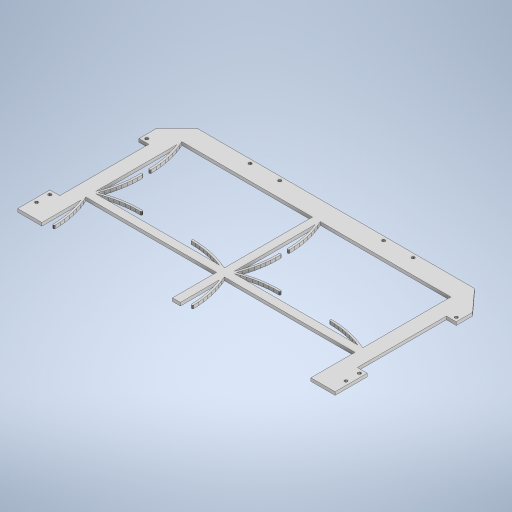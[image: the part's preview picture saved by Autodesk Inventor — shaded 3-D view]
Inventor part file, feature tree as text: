
AUTODESK INVENTOR PART (.ipt)
format: ipt  version: 2024.1 (Build 281209000, 209)  size: 804,864 bytes
history: native  units: in
note: dims shown in document units (in); Inventor stores cm internally (conversion verified against a paired STEP export)
features: extrude x1, sketch x1
ambient origin geometry x8: Origin, YZ Plane, XZ Plane, XY Plane, X Axis, Y Axis, Z Axis, Center Point
bodies: Solid1 (feature_tree)
feature tree (2):
  extrude  "Extrusion1"  [1 undecoded]
  sketch  "Sketch1"  dims[d0=0.125in d1=0.0in]
note: 1 required parameter value undecoded (feature->parameter linkage not recoverable at this tier; creation-order binding heuristic only, values carry confidence <= 0.55)
